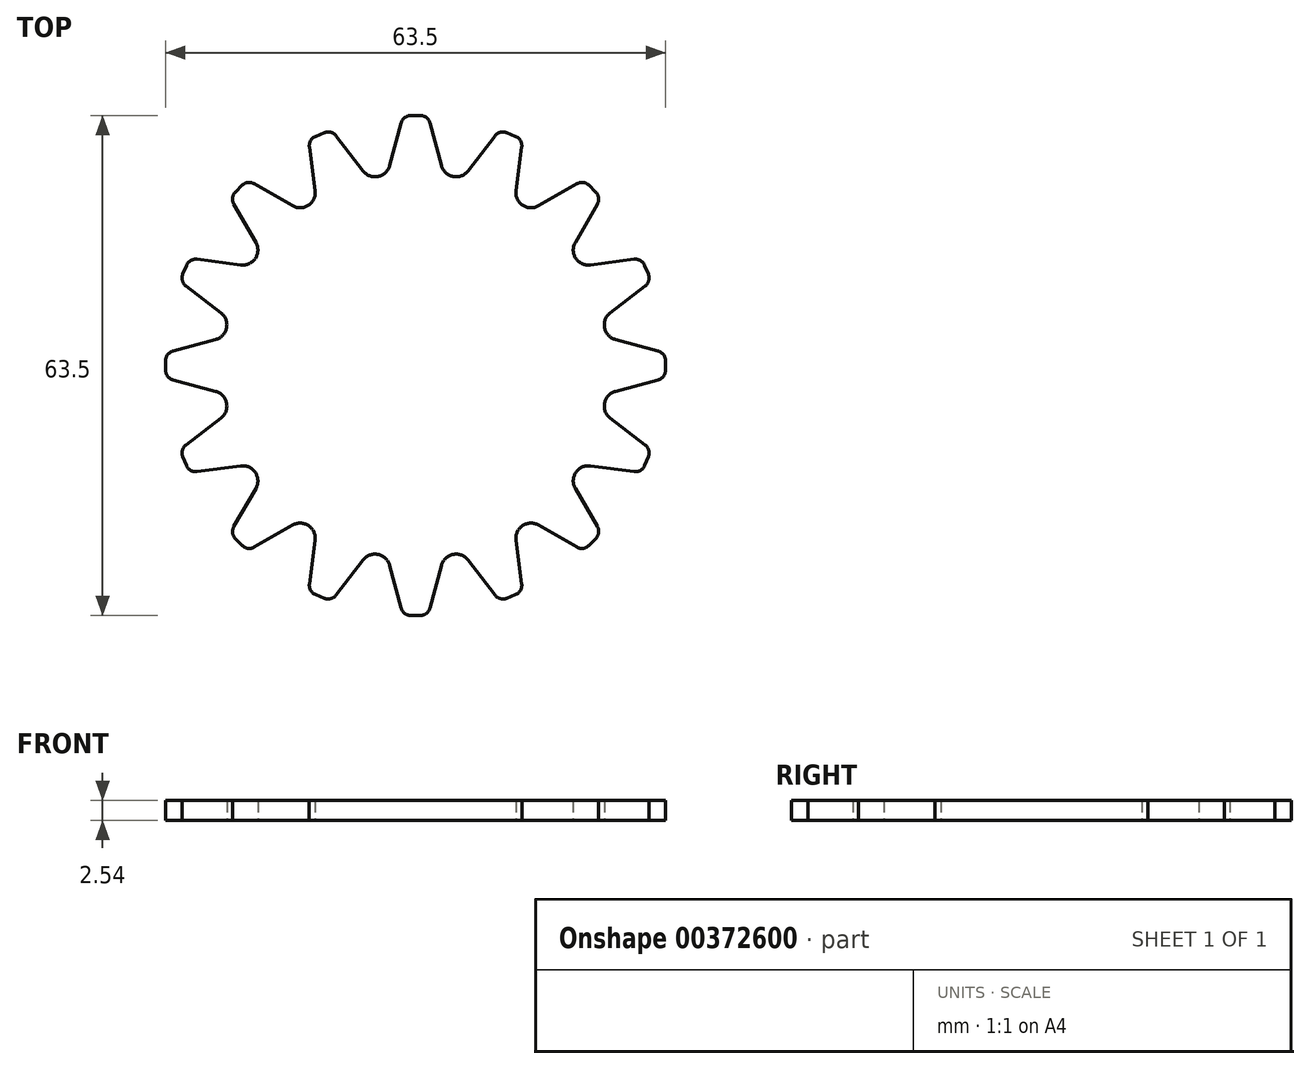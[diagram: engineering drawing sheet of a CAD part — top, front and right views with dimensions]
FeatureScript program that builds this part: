
annotation { "Feature Type Name" : "Feature", "Feature Type Description" : "" }
export const myFeature = defineFeature(function(context is Context, id is Id, definition is map)
    precondition{}
    {
        {
            var Q0;
            Q0=qCreatedBy(makeId("Top.planeOp"),FACE);
            var sketch = newSketch(context, id + "F0", { "sketchPlane" : qUnion([Q0])});
            skCircle(sketch, "E0", {"center": v(0, 0) * mm, "radius": 25.4 * mm, "construction": true});
            skLineSegment(sketch, "E1", {"start": v(0, 0) * mm, "end": v(0, -63.16) * mm, "construction": true});
            skLineSegment(sketch, "E2", {"start": v(3.29, -25.4) * mm, "end": v(1.84, -30.8) * mm});
            skLineSegment(sketch, "E3", {"start": v(0.61, -31.75) * mm, "end": v(0, -31.75) * mm});
            skPoint(sketch, "E4.visualSharp", {"position": v(1.59, -31.75) * mm});
            skArc(sketch, "E4.filletArc", {"start": v(0.61, -31.75) * mm, "mid": v(1.39, -31.49) * mm, "end": v(1.84, -30.8) * mm});
            skLineSegment(sketch, "E5.MirrorCS", {"start": v(-0.61, -31.75) * mm, "end": v(0, -31.75) * mm});
            skArc(sketch, "E6.MirrorCS", {"start": v(-0.61, -31.75) * mm, "mid": v(-1.39, -31.49) * mm, "end": v(-1.84, -30.8) * mm});
            skLineSegment(sketch, "E7.MirrorCS", {"start": v(-3.29, -25.4) * mm, "end": v(-1.84, -30.8) * mm});
            skPoint(sketch, "E8.MirrorP", {"position": v(-1.59, -31.75) * mm});
            skArc(sketch, "E9", {"start": v(-3.29, -25.4) * mm, "mid": v(-4.78, -24) * mm, "end": v(-6.68, -24.73) * mm});
            skPoint(sketch, "E10.1.0", {"position": v(10.68, -29.94) * mm});
            skArc(sketch, "E10.1.1", {"start": v(6.68, -24.73) * mm, "mid": v(4.78, -24) * mm, "end": v(3.29, -25.4) * mm});
            skPoint(sketch, "E10.1.2", {"position": v(13.62, -28.73) * mm});
            skLineSegment(sketch, "E10.1.3", {"start": v(6.68, -24.73) * mm, "end": v(10.1, -29.17) * mm});
            skLineSegment(sketch, "E10.1.4", {"start": v(12.76, -22.2) * mm, "end": v(13.49, -27.76) * mm});
            skArc(sketch, "E10.1.5", {"start": v(11.58, -29.57) * mm, "mid": v(10.77, -29.62) * mm, "end": v(10.1, -29.17) * mm});
            skArc(sketch, "E10.1.6", {"start": v(12.72, -29.1) * mm, "mid": v(13.33, -28.56) * mm, "end": v(13.49, -27.76) * mm});
            skLineSegment(sketch, "E10.1.7", {"start": v(11.58, -29.57) * mm, "end": v(12.15, -29.33) * mm});
            skLineSegment(sketch, "E10.1.8", {"start": v(12.72, -29.1) * mm, "end": v(12.15, -29.33) * mm});
            skPoint(sketch, "E10.2.0", {"position": v(21.33, -23.57) * mm});
            skArc(sketch, "E10.2.1", {"start": v(15.63, -20.29) * mm, "mid": v(13.6, -20.35) * mm, "end": v(12.76, -22.2) * mm});
            skPoint(sketch, "E10.2.2", {"position": v(23.57, -21.33) * mm});
            skLineSegment(sketch, "E10.2.3", {"start": v(15.63, -20.29) * mm, "end": v(20.48, -23.09) * mm});
            skLineSegment(sketch, "E10.2.4", {"start": v(20.29, -15.63) * mm, "end": v(23.09, -20.48) * mm});
            skArc(sketch, "E10.2.5", {"start": v(22.02, -22.88) * mm, "mid": v(21.28, -23.25) * mm, "end": v(20.48, -23.09) * mm});
            skArc(sketch, "E10.2.6", {"start": v(22.88, -22.02) * mm, "mid": v(23.25, -21.28) * mm, "end": v(23.09, -20.48) * mm});
            skLineSegment(sketch, "E10.2.7", {"start": v(22.02, -22.88) * mm, "end": v(22.45, -22.45) * mm});
            skLineSegment(sketch, "E10.2.8", {"start": v(22.88, -22.02) * mm, "end": v(22.45, -22.45) * mm});
            skPoint(sketch, "E10.3.0", {"position": v(28.73, -13.62) * mm});
            skArc(sketch, "E10.3.1", {"start": v(22.2, -12.76) * mm, "mid": v(20.35, -13.6) * mm, "end": v(20.29, -15.63) * mm});
            skPoint(sketch, "E10.3.2", {"position": v(29.94, -10.68) * mm});
            skLineSegment(sketch, "E10.3.3", {"start": v(22.2, -12.76) * mm, "end": v(27.76, -13.49) * mm});
            skLineSegment(sketch, "E10.3.4", {"start": v(24.73, -6.68) * mm, "end": v(29.17, -10.1) * mm});
            skArc(sketch, "E10.3.5", {"start": v(29.1, -12.72) * mm, "mid": v(28.56, -13.33) * mm, "end": v(27.76, -13.49) * mm});
            skArc(sketch, "E10.3.6", {"start": v(29.57, -11.58) * mm, "mid": v(29.62, -10.77) * mm, "end": v(29.17, -10.1) * mm});
            skLineSegment(sketch, "E10.3.7", {"start": v(29.1, -12.72) * mm, "end": v(29.33, -12.15) * mm});
            skLineSegment(sketch, "E10.3.8", {"start": v(29.57, -11.58) * mm, "end": v(29.33, -12.15) * mm});
            skPoint(sketch, "E10.4.0", {"position": v(31.75, -1.59) * mm});
            skArc(sketch, "E10.4.1", {"start": v(25.4, -3.29) * mm, "mid": v(24, -4.78) * mm, "end": v(24.73, -6.68) * mm});
            skPoint(sketch, "E10.4.2", {"position": v(31.75, 1.59) * mm});
            skLineSegment(sketch, "E10.4.3", {"start": v(25.4, -3.29) * mm, "end": v(30.8, -1.84) * mm});
            skLineSegment(sketch, "E10.4.4", {"start": v(25.4, 3.29) * mm, "end": v(30.8, 1.84) * mm});
            skArc(sketch, "E10.4.5", {"start": v(31.75, -0.61) * mm, "mid": v(31.49, -1.39) * mm, "end": v(30.8, -1.84) * mm});
            skArc(sketch, "E10.4.6", {"start": v(31.75, 0.61) * mm, "mid": v(31.49, 1.39) * mm, "end": v(30.8, 1.84) * mm});
            skLineSegment(sketch, "E10.4.7", {"start": v(31.75, -0.61) * mm, "end": v(31.75, 0) * mm});
            skLineSegment(sketch, "E10.4.8", {"start": v(31.75, 0.61) * mm, "end": v(31.75, 0) * mm});
            skPoint(sketch, "E10.5.0", {"position": v(29.94, 10.68) * mm});
            skArc(sketch, "E10.5.1", {"start": v(24.73, 6.68) * mm, "mid": v(24, 4.78) * mm, "end": v(25.4, 3.29) * mm});
            skPoint(sketch, "E10.5.2", {"position": v(28.73, 13.62) * mm});
            skLineSegment(sketch, "E10.5.3", {"start": v(24.73, 6.68) * mm, "end": v(29.17, 10.1) * mm});
            skLineSegment(sketch, "E10.5.4", {"start": v(22.2, 12.76) * mm, "end": v(27.76, 13.49) * mm});
            skArc(sketch, "E10.5.5", {"start": v(29.57, 11.58) * mm, "mid": v(29.62, 10.77) * mm, "end": v(29.17, 10.1) * mm});
            skArc(sketch, "E10.5.6", {"start": v(29.1, 12.72) * mm, "mid": v(28.56, 13.33) * mm, "end": v(27.76, 13.49) * mm});
            skLineSegment(sketch, "E10.5.7", {"start": v(29.57, 11.58) * mm, "end": v(29.33, 12.15) * mm});
            skLineSegment(sketch, "E10.5.8", {"start": v(29.1, 12.72) * mm, "end": v(29.33, 12.15) * mm});
            skPoint(sketch, "E10.6.0", {"position": v(23.57, 21.33) * mm});
            skArc(sketch, "E10.6.1", {"start": v(20.29, 15.63) * mm, "mid": v(20.35, 13.6) * mm, "end": v(22.2, 12.76) * mm});
            skPoint(sketch, "E10.6.2", {"position": v(21.33, 23.57) * mm});
            skLineSegment(sketch, "E10.6.3", {"start": v(20.29, 15.63) * mm, "end": v(23.09, 20.48) * mm});
            skLineSegment(sketch, "E10.6.4", {"start": v(15.63, 20.29) * mm, "end": v(20.48, 23.09) * mm});
            skArc(sketch, "E10.6.5", {"start": v(22.88, 22.02) * mm, "mid": v(23.25, 21.28) * mm, "end": v(23.09, 20.48) * mm});
            skArc(sketch, "E10.6.6", {"start": v(22.02, 22.88) * mm, "mid": v(21.28, 23.25) * mm, "end": v(20.48, 23.09) * mm});
            skLineSegment(sketch, "E10.6.7", {"start": v(22.88, 22.02) * mm, "end": v(22.45, 22.45) * mm});
            skLineSegment(sketch, "E10.6.8", {"start": v(22.02, 22.88) * mm, "end": v(22.45, 22.45) * mm});
            skPoint(sketch, "E10.7.0", {"position": v(13.62, 28.73) * mm});
            skArc(sketch, "E10.7.1", {"start": v(12.76, 22.2) * mm, "mid": v(13.6, 20.35) * mm, "end": v(15.63, 20.29) * mm});
            skPoint(sketch, "E10.7.2", {"position": v(10.68, 29.94) * mm});
            skLineSegment(sketch, "E10.7.3", {"start": v(12.76, 22.2) * mm, "end": v(13.49, 27.76) * mm});
            skLineSegment(sketch, "E10.7.4", {"start": v(6.68, 24.73) * mm, "end": v(10.1, 29.17) * mm});
            skArc(sketch, "E10.7.5", {"start": v(12.72, 29.1) * mm, "mid": v(13.33, 28.56) * mm, "end": v(13.49, 27.76) * mm});
            skArc(sketch, "E10.7.6", {"start": v(11.58, 29.57) * mm, "mid": v(10.77, 29.62) * mm, "end": v(10.1, 29.17) * mm});
            skLineSegment(sketch, "E10.7.7", {"start": v(12.72, 29.1) * mm, "end": v(12.15, 29.33) * mm});
            skLineSegment(sketch, "E10.7.8", {"start": v(11.58, 29.57) * mm, "end": v(12.15, 29.33) * mm});
            skPoint(sketch, "E10.8.0", {"position": v(1.59, 31.75) * mm});
            skArc(sketch, "E10.8.1", {"start": v(3.29, 25.4) * mm, "mid": v(4.78, 24) * mm, "end": v(6.68, 24.73) * mm});
            skPoint(sketch, "E10.8.2", {"position": v(-1.59, 31.75) * mm});
            skLineSegment(sketch, "E10.8.3", {"start": v(3.29, 25.4) * mm, "end": v(1.84, 30.8) * mm});
            skLineSegment(sketch, "E10.8.4", {"start": v(-3.29, 25.4) * mm, "end": v(-1.84, 30.8) * mm});
            skArc(sketch, "E10.8.5", {"start": v(0.61, 31.75) * mm, "mid": v(1.39, 31.49) * mm, "end": v(1.84, 30.8) * mm});
            skArc(sketch, "E10.8.6", {"start": v(-0.61, 31.75) * mm, "mid": v(-1.39, 31.49) * mm, "end": v(-1.84, 30.8) * mm});
            skLineSegment(sketch, "E10.8.7", {"start": v(0.61, 31.75) * mm, "end": v(0, 31.75) * mm});
            skLineSegment(sketch, "E10.8.8", {"start": v(-0.61, 31.75) * mm, "end": v(0, 31.75) * mm});
            skPoint(sketch, "E10.9.0", {"position": v(-10.68, 29.94) * mm});
            skArc(sketch, "E10.9.1", {"start": v(-6.68, 24.73) * mm, "mid": v(-4.78, 24) * mm, "end": v(-3.29, 25.4) * mm});
            skPoint(sketch, "E10.9.2", {"position": v(-13.62, 28.73) * mm});
            skLineSegment(sketch, "E10.9.3", {"start": v(-6.68, 24.73) * mm, "end": v(-10.1, 29.17) * mm});
            skLineSegment(sketch, "E10.9.4", {"start": v(-12.76, 22.2) * mm, "end": v(-13.49, 27.76) * mm});
            skArc(sketch, "E10.9.5", {"start": v(-11.58, 29.57) * mm, "mid": v(-10.77, 29.62) * mm, "end": v(-10.1, 29.17) * mm});
            skArc(sketch, "E10.9.6", {"start": v(-12.72, 29.1) * mm, "mid": v(-13.33, 28.56) * mm, "end": v(-13.49, 27.76) * mm});
            skLineSegment(sketch, "E10.9.7", {"start": v(-11.58, 29.57) * mm, "end": v(-12.15, 29.33) * mm});
            skLineSegment(sketch, "E10.9.8", {"start": v(-12.72, 29.1) * mm, "end": v(-12.15, 29.33) * mm});
            skPoint(sketch, "E10.10.0", {"position": v(-21.33, 23.57) * mm});
            skArc(sketch, "E10.10.1", {"start": v(-15.63, 20.29) * mm, "mid": v(-13.6, 20.35) * mm, "end": v(-12.76, 22.2) * mm});
            skPoint(sketch, "E10.10.2", {"position": v(-23.57, 21.33) * mm});
            skLineSegment(sketch, "E10.10.3", {"start": v(-15.63, 20.29) * mm, "end": v(-20.48, 23.09) * mm});
            skLineSegment(sketch, "E10.10.4", {"start": v(-20.29, 15.63) * mm, "end": v(-23.09, 20.48) * mm});
            skArc(sketch, "E10.10.5", {"start": v(-22.02, 22.88) * mm, "mid": v(-21.28, 23.25) * mm, "end": v(-20.48, 23.09) * mm});
            skArc(sketch, "E10.10.6", {"start": v(-22.88, 22.02) * mm, "mid": v(-23.25, 21.28) * mm, "end": v(-23.09, 20.48) * mm});
            skLineSegment(sketch, "E10.10.7", {"start": v(-22.02, 22.88) * mm, "end": v(-22.45, 22.45) * mm});
            skLineSegment(sketch, "E10.10.8", {"start": v(-22.88, 22.02) * mm, "end": v(-22.45, 22.45) * mm});
            skPoint(sketch, "E10.11.0", {"position": v(-28.73, 13.62) * mm});
            skArc(sketch, "E10.11.1", {"start": v(-22.2, 12.76) * mm, "mid": v(-20.35, 13.6) * mm, "end": v(-20.29, 15.63) * mm});
            skPoint(sketch, "E10.11.2", {"position": v(-29.94, 10.68) * mm});
            skLineSegment(sketch, "E10.11.3", {"start": v(-22.2, 12.76) * mm, "end": v(-27.76, 13.49) * mm});
            skLineSegment(sketch, "E10.11.4", {"start": v(-24.73, 6.68) * mm, "end": v(-29.17, 10.1) * mm});
            skArc(sketch, "E10.11.5", {"start": v(-29.1, 12.72) * mm, "mid": v(-28.56, 13.33) * mm, "end": v(-27.76, 13.49) * mm});
            skArc(sketch, "E10.11.6", {"start": v(-29.57, 11.58) * mm, "mid": v(-29.62, 10.77) * mm, "end": v(-29.17, 10.1) * mm});
            skLineSegment(sketch, "E10.11.7", {"start": v(-29.1, 12.72) * mm, "end": v(-29.33, 12.15) * mm});
            skLineSegment(sketch, "E10.11.8", {"start": v(-29.57, 11.58) * mm, "end": v(-29.33, 12.15) * mm});
            skPoint(sketch, "E10.12.0", {"position": v(-31.75, 1.59) * mm});
            skArc(sketch, "E10.12.1", {"start": v(-25.4, 3.29) * mm, "mid": v(-24, 4.78) * mm, "end": v(-24.73, 6.68) * mm});
            skPoint(sketch, "E10.12.2", {"position": v(-31.75, -1.59) * mm});
            skLineSegment(sketch, "E10.12.3", {"start": v(-25.4, 3.29) * mm, "end": v(-30.8, 1.84) * mm});
            skLineSegment(sketch, "E10.12.4", {"start": v(-25.4, -3.29) * mm, "end": v(-30.8, -1.84) * mm});
            skArc(sketch, "E10.12.5", {"start": v(-31.75, 0.61) * mm, "mid": v(-31.49, 1.39) * mm, "end": v(-30.8, 1.84) * mm});
            skArc(sketch, "E10.12.6", {"start": v(-31.75, -0.61) * mm, "mid": v(-31.49, -1.39) * mm, "end": v(-30.8, -1.84) * mm});
            skLineSegment(sketch, "E10.12.7", {"start": v(-31.75, 0.61) * mm, "end": v(-31.75, 0) * mm});
            skLineSegment(sketch, "E10.12.8", {"start": v(-31.75, -0.61) * mm, "end": v(-31.75, 0) * mm});
            skPoint(sketch, "E10.13.0", {"position": v(-29.94, -10.68) * mm});
            skArc(sketch, "E10.13.1", {"start": v(-24.73, -6.68) * mm, "mid": v(-24, -4.78) * mm, "end": v(-25.4, -3.29) * mm});
            skPoint(sketch, "E10.13.2", {"position": v(-28.73, -13.62) * mm});
            skLineSegment(sketch, "E10.13.3", {"start": v(-24.73, -6.68) * mm, "end": v(-29.17, -10.1) * mm});
            skLineSegment(sketch, "E10.13.4", {"start": v(-22.2, -12.76) * mm, "end": v(-27.76, -13.49) * mm});
            skArc(sketch, "E10.13.5", {"start": v(-29.57, -11.58) * mm, "mid": v(-29.62, -10.77) * mm, "end": v(-29.17, -10.1) * mm});
            skArc(sketch, "E10.13.6", {"start": v(-29.1, -12.72) * mm, "mid": v(-28.56, -13.33) * mm, "end": v(-27.76, -13.49) * mm});
            skLineSegment(sketch, "E10.13.7", {"start": v(-29.57, -11.58) * mm, "end": v(-29.33, -12.15) * mm});
            skLineSegment(sketch, "E10.13.8", {"start": v(-29.1, -12.72) * mm, "end": v(-29.33, -12.15) * mm});
            skPoint(sketch, "E10.14.0", {"position": v(-23.57, -21.33) * mm});
            skArc(sketch, "E10.14.1", {"start": v(-20.29, -15.63) * mm, "mid": v(-20.35, -13.6) * mm, "end": v(-22.2, -12.76) * mm});
            skPoint(sketch, "E10.14.2", {"position": v(-21.33, -23.57) * mm});
            skLineSegment(sketch, "E10.14.3", {"start": v(-20.29, -15.63) * mm, "end": v(-23.09, -20.48) * mm});
            skLineSegment(sketch, "E10.14.4", {"start": v(-15.63, -20.29) * mm, "end": v(-20.48, -23.09) * mm});
            skArc(sketch, "E10.14.5", {"start": v(-22.88, -22.02) * mm, "mid": v(-23.25, -21.28) * mm, "end": v(-23.09, -20.48) * mm});
            skArc(sketch, "E10.14.6", {"start": v(-22.02, -22.88) * mm, "mid": v(-21.28, -23.25) * mm, "end": v(-20.48, -23.09) * mm});
            skLineSegment(sketch, "E10.14.7", {"start": v(-22.88, -22.02) * mm, "end": v(-22.45, -22.45) * mm});
            skLineSegment(sketch, "E10.14.8", {"start": v(-22.02, -22.88) * mm, "end": v(-22.45, -22.45) * mm});
            skPoint(sketch, "E10.15.0", {"position": v(-13.62, -28.73) * mm});
            skArc(sketch, "E10.15.1", {"start": v(-12.76, -22.2) * mm, "mid": v(-13.6, -20.35) * mm, "end": v(-15.63, -20.29) * mm});
            skPoint(sketch, "E10.15.2", {"position": v(-10.68, -29.94) * mm});
            skLineSegment(sketch, "E10.15.3", {"start": v(-12.76, -22.2) * mm, "end": v(-13.49, -27.76) * mm});
            skLineSegment(sketch, "E10.15.4", {"start": v(-6.68, -24.73) * mm, "end": v(-10.1, -29.17) * mm});
            skArc(sketch, "E10.15.5", {"start": v(-12.72, -29.1) * mm, "mid": v(-13.33, -28.56) * mm, "end": v(-13.49, -27.76) * mm});
            skArc(sketch, "E10.15.6", {"start": v(-11.58, -29.57) * mm, "mid": v(-10.77, -29.62) * mm, "end": v(-10.1, -29.17) * mm});
            skLineSegment(sketch, "E10.15.7", {"start": v(-12.72, -29.1) * mm, "end": v(-12.15, -29.33) * mm});
            skLineSegment(sketch, "E10.15.8", {"start": v(-11.58, -29.57) * mm, "end": v(-12.15, -29.33) * mm});
            skSolve(sketch);
        }
        {
            var Q0;
            Q0=makeQuery(id+"F0.imprint","IMPRINT",FACE,{"disambiguationData":[TD([[makeQuery(id+"F0.imprint","IMPRINT",EDGE,{"derivedFrom":sQuery(id+"F0.wireOp",EDGE,"E2")}),-1.0]])]});
            extrude(context, id + "F1", {"entities" : qUnion([Q0]), "depth" : 2.54 * mm});
        }
    });
